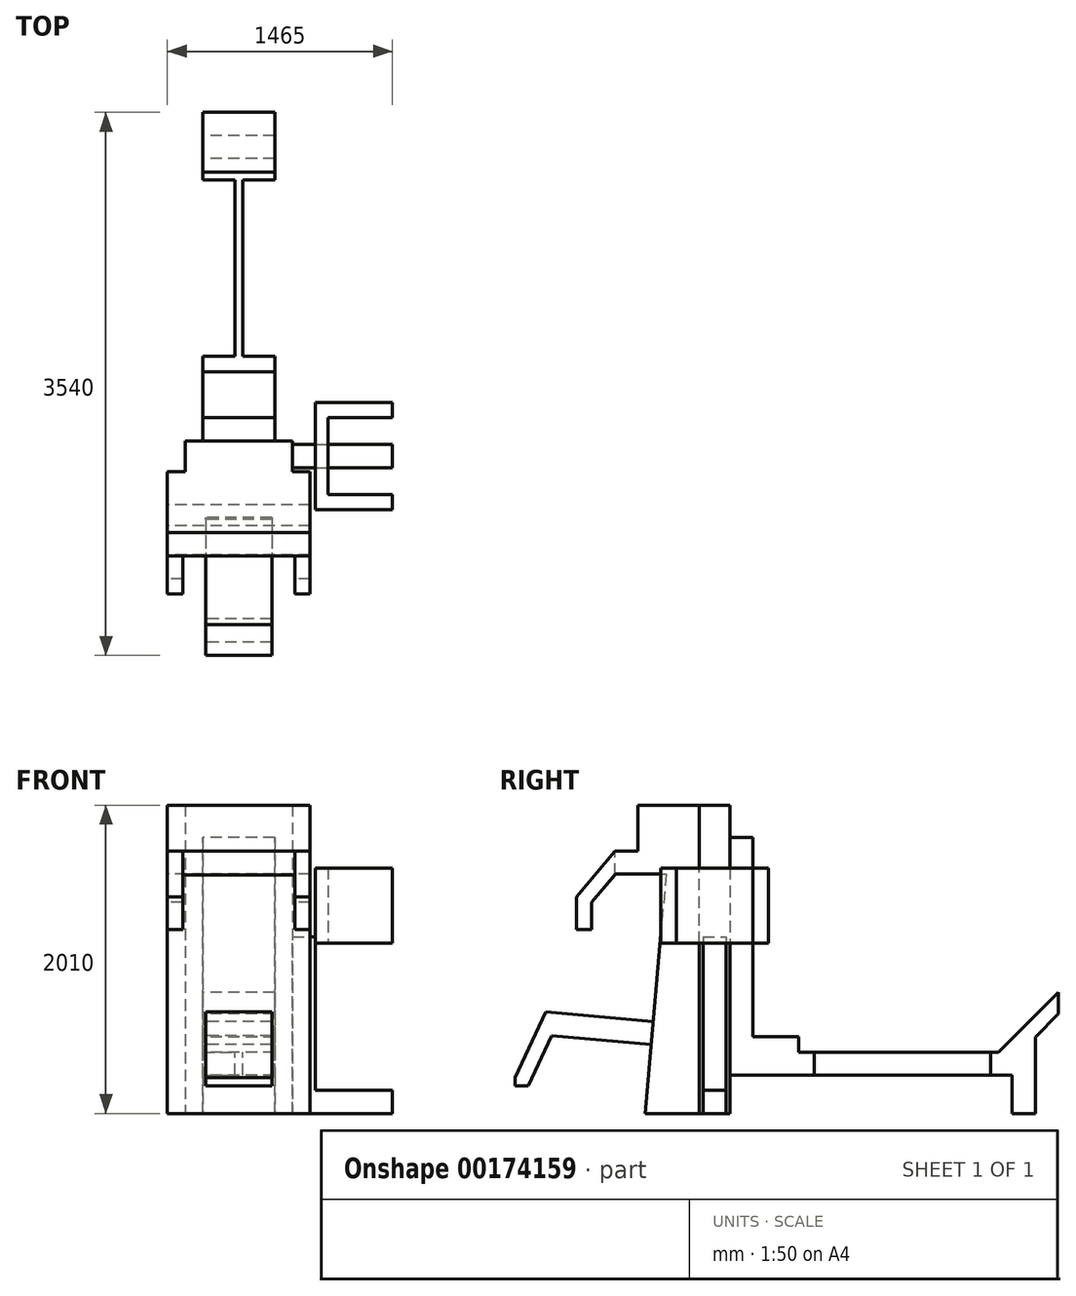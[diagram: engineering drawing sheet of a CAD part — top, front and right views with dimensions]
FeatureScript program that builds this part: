
annotation { "Feature Type Name" : "Feature", "Feature Type Description" : "" }
export const myFeature = defineFeature(function(context is Context, id is Id, definition is map)
    precondition{}
    {
        {
            var Q0;
            Q0=qCreatedBy(makeId("Top.planeOp"),FACE);
            var sketch = newSketch(context, id + "F0", { "sketchPlane" : qUnion([Q0])});
            skLineSegment(sketch, "E0.bottom", {"start": v(-350, 100) * mm, "end": v(350, 100) * mm});
            skLineSegment(sketch, "E0.top", {"start": v(-350, -100) * mm, "end": v(350, -100) * mm});
            skLineSegment(sketch, "E0.left", {"start": v(-350, 100) * mm, "end": v(-350, -100) * mm});
            skLineSegment(sketch, "E0.right", {"start": v(350, 100) * mm, "end": v(350, -100) * mm});
            skSolve(sketch);
        }
        {
            var Q0;
            Q0=makeQuery(id+"F0.imprint","IMPRINT",FACE,{"disambiguationData":[TD([[makeQuery(id+"F0.imprint","IMPRINT",EDGE,{"derivedFrom":sQuery(id+"F0.wireOp",EDGE,"E0.bottom")}),-1.0]])]});
            extrude(context, id + "F1", {"entities" : qUnion([Q0]), "depth" : 2010 * mm});
        }
        {
            var Q0;
            Q0=qCreatedBy(makeId("Front.planeOp"),FACE);
            var sketch = newSketch(context, id + "F2", { "sketchPlane" : qUnion([Q0])});
            skLineSegment(sketch, "E1", {"start": v(350, 1150) * mm, "end": v(500, 1150) * mm});
            skLineSegment(sketch, "E2", {"start": v(500, 1150) * mm, "end": v(500, 150) * mm});
            skLineSegment(sketch, "E3", {"start": v(500, 150) * mm, "end": v(1000, 150) * mm});
            skLineSegment(sketch, "E4", {"start": v(1000, 150) * mm, "end": v(1000, 0) * mm});
            skLineSegment(sketch, "E5", {"start": v(1000, 0) * mm, "end": v(350, 0) * mm});
            skLineSegment(sketch, "E6", {"start": v(350, 0) * mm, "end": v(350, 1150) * mm});
            skSolve(sketch);
        }
        {
            var Q0;
            Q0=qSketchRegion(id+"F2",true);
            extrude(context, id + "F3", {"entities" : qUnion([Q0]), "operationType" : NewBodyOperationType.ADD, "endBound" : BoundingType.SYMMETRIC, "depth" : 150 * mm});
        }
        {
            var Q0;
            Q0=makeQuery(id+"F3.opExtrude","SWEPT_FACE",FACE,{"disambiguationData":[OSD([sQuery(id+"F2.wireOp",EDGE,"E1")])]});
            var sketch = newSketch(context, id + "F4", { "sketchPlane" : qUnion([Q0])});
            skLineSegment(sketch, "E7", {"start": v(500, 350) * mm, "end": v(1000, 350) * mm});
            skLineSegment(sketch, "E8", {"start": v(1000, 350) * mm, "end": v(1000, 250) * mm});
            skLineSegment(sketch, "E9", {"start": v(1000, 250) * mm, "end": v(580, 250) * mm});
            skLineSegment(sketch, "E10", {"start": v(580, 250) * mm, "end": v(580, 0) * mm});
            skPoint(sketch, "E10.endSnap0", {"position": v(500, 0) * mm});
            skLineSegment(sketch, "E11", {"start": v(500, 0) * mm, "end": v(1378.85, 0) * mm, "construction": true});
            skLineSegment(sketch, "E12.MirrorCS", {"start": v(500, -350) * mm, "end": v(1000, -350) * mm});
            skLineSegment(sketch, "E13.MirrorCS", {"start": v(1000, -350) * mm, "end": v(1000, -250) * mm});
            skLineSegment(sketch, "E14.MirrorCS", {"start": v(1000, -250) * mm, "end": v(580, -250) * mm});
            skLineSegment(sketch, "E15.MirrorCS", {"start": v(580, -250) * mm, "end": v(580, 0) * mm});
            skLineSegment(sketch, "E16", {"start": v(500, 0) * mm, "end": v(500, 350) * mm});
            skLineSegment(sketch, "E17.MirrorCS", {"start": v(500, 0) * mm, "end": v(500, -350) * mm});
            skSolve(sketch);
        }
        {
            var Q0;
            Q0=qCreatedBy(makeId("Right.planeOp"),FACE);
            var sketch = newSketch(context, id + "F5", { "sketchPlane" : qUnion([Q0])});
            skLineSegment(sketch, "E18", {"start": v(-100, 2010) * mm, "end": v(-500, 2010) * mm});
            skLineSegment(sketch, "E19", {"start": v(-500, 2010) * mm, "end": v(-500, 1710) * mm});
            skLineSegment(sketch, "E20", {"start": v(-500, 1710) * mm, "end": v(-650, 1710) * mm});
            skLineSegment(sketch, "E21", {"start": v(-650, 1710) * mm, "end": v(-900, 1412.06) * mm});
            skLineSegment(sketch, "E22", {"start": v(-900, 1412.06) * mm, "end": v(-900, 1200) * mm});
            skLineSegment(sketch, "E23", {"start": v(-900, 1200) * mm, "end": v(-800, 1200) * mm});
            skLineSegment(sketch, "E24", {"start": v(-800, 1200) * mm, "end": v(-800, 1375.66) * mm});
            skLineSegment(sketch, "E25", {"start": v(-800, 1375.66) * mm, "end": v(-645.32, 1560) * mm});
            skLineSegment(sketch, "E26", {"start": v(-645.32, 1560) * mm, "end": v(-316.01, 1560) * mm});
            skLineSegment(sketch, "E27", {"start": v(-316.01, 1560) * mm, "end": v(-400, 600) * mm});
            skLineSegment(sketch, "E28", {"start": v(-400, 600) * mm, "end": v(-1100, 661.24) * mm});
            skLineSegment(sketch, "E29", {"start": v(-1100, 661.24) * mm, "end": v(-1300, 232.34) * mm});
            skLineSegment(sketch, "E30", {"start": v(-1300, 232.34) * mm, "end": v(-1300, 180) * mm});
            skLineSegment(sketch, "E31", {"start": v(-1300, 180) * mm, "end": v(-1214.07, 180) * mm});
            skLineSegment(sketch, "E32", {"start": v(-1214.07, 180) * mm, "end": v(-1061.45, 507.3) * mm});
            skLineSegment(sketch, "E33", {"start": v(-1061.45, 507.3) * mm, "end": v(-413.07, 450.57) * mm});
            skLineSegment(sketch, "E34", {"start": v(-413.07, 450.57) * mm, "end": v(-452.5, 0) * mm});
            skLineSegment(sketch, "E35", {"start": v(-452.5, 0) * mm, "end": v(-100, 0) * mm});
            skLineSegment(sketch, "E36", {"start": v(-100, 0) * mm, "end": v(-100, 2010) * mm});
            skSolve(sketch);
        }
        {
            var Q0;
            Q0=makeQuery(id+"F5.imprint","IMPRINT",FACE,{"disambiguationData":[TD([[makeQuery(id+"F5.imprint","IMPRINT",EDGE,{"derivedFrom":sQuery(id+"F5.wireOp",EDGE,"E18")}),1.0]])]});
            extrude(context, id + "F6", {"entities" : qUnion([Q0]), "operationType" : NewBodyOperationType.ADD, "endBound" : BoundingType.SYMMETRIC, "depth" : 930 * mm});
        }
        {
            var Q0;
            Q0=makeQuery(id+"F6.opExtrude","SWEPT_FACE",FACE,{"disambiguationData":[OSD([sQuery(id+"F5.wireOp",EDGE,"E20")])]});
            var sketch = newSketch(context, id + "F7", { "sketchPlane" : qUnion([Q0])});
            skLineSegment(sketch, "E37.bottom", {"start": v(-365, -500) * mm, "end": v(365, -500) * mm});
            skLineSegment(sketch, "E37.top", {"start": v(-365, -900) * mm, "end": v(365, -900) * mm});
            skLineSegment(sketch, "E37.left", {"start": v(-365, -500) * mm, "end": v(-365, -900) * mm});
            skLineSegment(sketch, "E37.right", {"start": v(365, -500) * mm, "end": v(365, -900) * mm});
            skSolve(sketch);
        }
        {
            var Q0;
            {var subQ0=sQuery(id+"F7.wireOp",EDGE,"E37.top");Q0=makeQuery(id+"F7.imprint","IMPRINT",FACE,{"disambiguationData":[TD([[makeQuery(id+"F7.imprint","IMPRINT",EDGE,{"derivedFrom":subQ0}),1.0]])]});}
            var Q1;
            Q1=makeQuery(id+"F6.opExtrude","SWEPT_FACE",FACE,{"disambiguationData":[OSD([sQuery(id+"F5.wireOp",EDGE,"E23")])]});
            extrude(context, id + "F8", {"entities" : qUnion([Q0]), "operationType" : NewBodyOperationType.REMOVE, "endBound" : BoundingType.UP_TO_SURFACE, "oppositeDirection" : true, "endBoundEntityFace" : qUnion([Q1]), "depth" : 25 * mm});
        }
        {
            var Q0;
            Q0=qCreatedBy(makeId("Right.planeOp"),FACE);
            var sketch = newSketch(context, id + "F9", { "sketchPlane" : qUnion([Q0])});
            skLineSegment(sketch, "E38", {"start": v(100, 250) * mm, "end": v(1940, 250) * mm});
            skLineSegment(sketch, "E39", {"start": v(1940, 250) * mm, "end": v(1940, 0) * mm});
            skLineSegment(sketch, "E40", {"start": v(1940, 0) * mm, "end": v(2090, 0) * mm});
            skLineSegment(sketch, "E41", {"start": v(2090, 0) * mm, "end": v(2090, 498.58) * mm});
            skLineSegment(sketch, "E42", {"start": v(2090, 498.58) * mm, "end": v(2240, 648.58) * mm});
            skLineSegment(sketch, "E43", {"start": v(2240, 648.58) * mm, "end": v(2240, 790) * mm});
            skLineSegment(sketch, "E44", {"start": v(2240, 790) * mm, "end": v(1850, 400) * mm});
            skLineSegment(sketch, "E45", {"start": v(1850, 400) * mm, "end": v(550, 400) * mm});
            skLineSegment(sketch, "E46", {"start": v(550, 400) * mm, "end": v(550, 500) * mm});
            skLineSegment(sketch, "E47", {"start": v(550, 500) * mm, "end": v(250, 500) * mm});
            skLineSegment(sketch, "E48", {"start": v(250, 500) * mm, "end": v(250, 1800) * mm});
            skLineSegment(sketch, "E49", {"start": v(250, 1800) * mm, "end": v(100, 1800) * mm});
            skLineSegment(sketch, "E50", {"start": v(100, 1800) * mm, "end": v(100, 250) * mm});
            skSolve(sketch);
        }
        {
            var Q0;
            Q0=makeQuery(id+"F9.imprint","IMPRINT",FACE,{"disambiguationData":[TD([[makeQuery(id+"F9.imprint","IMPRINT",EDGE,{"derivedFrom":sQuery(id+"F9.wireOp",EDGE,"E38")}),1.0]])]});
            extrude(context, id + "F10", {"entities" : qUnion([Q0]), "operationType" : NewBodyOperationType.ADD, "endBound" : BoundingType.SYMMETRIC, "depth" : 470 * mm});
        }
        {
            var Q0;
            {var subQ5=sQuery(id+"F4.wireOp",EDGE,"E7");Q0=makeQuery(id+"F4.imprint","IMPRINT",FACE,{"disambiguationData":[TD([[makeQuery(id+"F4.imprint","IMPRINT",EDGE,{"derivedFrom":subQ5}),-1.0]])]});}
            extrude(context, id + "F11", {"entities" : qUnion([Q0]), "operationType" : NewBodyOperationType.ADD, "depth" : 450 * mm, "hasSecondDirection" : true, "secondDirectionOppositeDirection" : true, "secondDirectionDepth" : 40 * mm});
        }
        {
            var Q0;
            Q0=makeQuery(id+"F6.opExtrude","SWEPT_FACE",FACE,{"disambiguationData":[OSD([sQuery(id+"F5.wireOp",EDGE,"E28")])]});
            var sketch = newSketch(context, id + "F12", { "sketchPlane" : qUnion([Q0])});
            skLineSegment(sketch, "E51.bottom", {"start": v(-465, -450.77) * mm, "end": v(-215, -450.77) * mm});
            skLineSegment(sketch, "E51.top", {"start": v(-465, -1315.3) * mm, "end": v(-215, -1315.3) * mm});
            skLineSegment(sketch, "E51.left", {"start": v(-465, -450.77) * mm, "end": v(-465, -1315.3) * mm});
            skLineSegment(sketch, "E51.right", {"start": v(-215, -450.77) * mm, "end": v(-215, -1315.3) * mm});
            skLineSegment(sketch, "E52", {"start": v(0, 0) * mm, "end": v(0, -1667.11) * mm, "construction": true});
            skLineSegment(sketch, "E53.MirrorCS", {"start": v(465, -450.77) * mm, "end": v(215, -450.77) * mm});
            skLineSegment(sketch, "E54.MirrorCS", {"start": v(215, -450.77) * mm, "end": v(215, -1315.3) * mm});
            skLineSegment(sketch, "E55.MirrorCS", {"start": v(465, -450.77) * mm, "end": v(465, -1315.3) * mm});
            skLineSegment(sketch, "E56.MirrorCS", {"start": v(465, -1315.3) * mm, "end": v(215, -1315.3) * mm});
            skSolve(sketch);
        }
        {
            var Q0;
            {var subQ0=sQuery(id+"F12.wireOp",EDGE,"E51.bottom");Q0=makeQuery(id+"F12.imprint","IMPRINT",FACE,{"disambiguationData":[TD([[makeQuery(id+"F12.imprint","IMPRINT",EDGE,{"derivedFrom":subQ0}),1.0]])]});}
            var Q1;
            {var subQ0=sQuery(id+"F12.wireOp",EDGE,"E51.top");Q1=makeQuery(id+"F12.imprint","IMPRINT",FACE,{"disambiguationData":[TD([[makeQuery(id+"F12.imprint","IMPRINT",EDGE,{"derivedFrom":subQ0}),1.0]])]});}
            var Q2;
            {var subQ0=sQuery(id+"F12.wireOp",EDGE,"E53.MirrorCS");Q2=makeQuery(id+"F12.imprint","IMPRINT",FACE,{"disambiguationData":[TD([[makeQuery(id+"F12.imprint","IMPRINT",EDGE,{"derivedFrom":subQ0}),1.0]])]});}
            var Q3;
            {var subQ0=sQuery(id+"F12.wireOp",EDGE,"E56.MirrorCS");Q3=makeQuery(id+"F12.imprint","IMPRINT",FACE,{"disambiguationData":[TD([[makeQuery(id+"F12.imprint","IMPRINT",EDGE,{"derivedFrom":subQ0}),-1.0]])]});}
            var Q4;
            Q4=makeQuery(id+"F6.boolean.opBoolean","MERGE",FACE,{"derivedFrom":[makeQuery(id+"F3.boolean.opBoolean","MERGE",FACE,{"derivedFrom":[makeQuery(id+"F1.opExtrude","CAP_FACE",FACE,{"disambiguationData":[OSD([sQuery(id+"F0.wireOp",EDGE,"E0.bottom"),sQuery(id+"F0.wireOp",EDGE,"E0.top"),sQuery(id+"F0.wireOp",EDGE,"E0.left"),sQuery(id+"F0.wireOp",EDGE,"E0.right")])],"isStart":true}),makeQuery(id+"F3.opExtrude","SWEPT_FACE",FACE,{"disambiguationData":[OSD([sQuery(id+"F2.wireOp",EDGE,"E5")])]})]}),makeQuery(id+"F6.opExtrude","SWEPT_FACE",FACE,{"disambiguationData":[OSD([sQuery(id+"F5.wireOp",EDGE,"E35")])]})]});
            extrude(context, id + "F13", {"entities" : qUnion([Q0, Q1, Q2, Q3]), "operationType" : NewBodyOperationType.REMOVE, "endBound" : BoundingType.UP_TO_SURFACE, "oppositeDirection" : true, "endBoundEntityFace" : qUnion([Q4]), "depth" : 25 * mm});
        }
        {
            var Q0;
            Q0=makeQuery(id+"F10.opExtrude","SWEPT_FACE",FACE,{"disambiguationData":[OSD([sQuery(id+"F9.wireOp",EDGE,"E45")])]});
            var sketch = newSketch(context, id + "F14", { "sketchPlane" : qUnion([Q0])});
            skLineSegment(sketch, "E57.bottom", {"start": v(-235, 1800) * mm, "end": v(-25, 1800) * mm});
            skLineSegment(sketch, "E57.top", {"start": v(-235, 650) * mm, "end": v(-25, 650) * mm});
            skLineSegment(sketch, "E57.left", {"start": v(-235, 1800) * mm, "end": v(-235, 650) * mm});
            skLineSegment(sketch, "E57.right", {"start": v(-25, 1800) * mm, "end": v(-25, 650) * mm});
            skLineSegment(sketch, "E58", {"start": v(0, 0) * mm, "end": v(0, 1985.23) * mm, "construction": true});
            skLineSegment(sketch, "E59.MirrorCS", {"start": v(25, 1800) * mm, "end": v(25, 650) * mm});
            skLineSegment(sketch, "E60.MirrorCS", {"start": v(235, 1800) * mm, "end": v(25, 1800) * mm});
            skLineSegment(sketch, "E61.MirrorCS", {"start": v(235, 650) * mm, "end": v(25, 650) * mm});
            skLineSegment(sketch, "E62.MirrorCS", {"start": v(235, 1800) * mm, "end": v(235, 650) * mm});
            skSolve(sketch);
        }
        {
            var Q0;
            Q0=makeQuery(id+"F14.imprint","IMPRINT",FACE,{"disambiguationData":[TD([[makeQuery(id+"F14.imprint","IMPRINT",EDGE,{"derivedFrom":sQuery(id+"F14.wireOp",EDGE,"E57.bottom")}),-1.0]])]});
            var Q1;
            Q1=makeQuery(id+"F14.imprint","IMPRINT",FACE,{"disambiguationData":[TD([[makeQuery(id+"F14.imprint","IMPRINT",EDGE,{"derivedFrom":sQuery(id+"F14.wireOp",EDGE,"E59.MirrorCS")}),1.0]])]});
            extrude(context, id + "F15", {"entities" : qUnion([Q0, Q1]), "operationType" : NewBodyOperationType.REMOVE, "endBound" : BoundingType.THROUGH_ALL, "oppositeDirection" : true, "depth" : 25 * mm});
        }
    });
